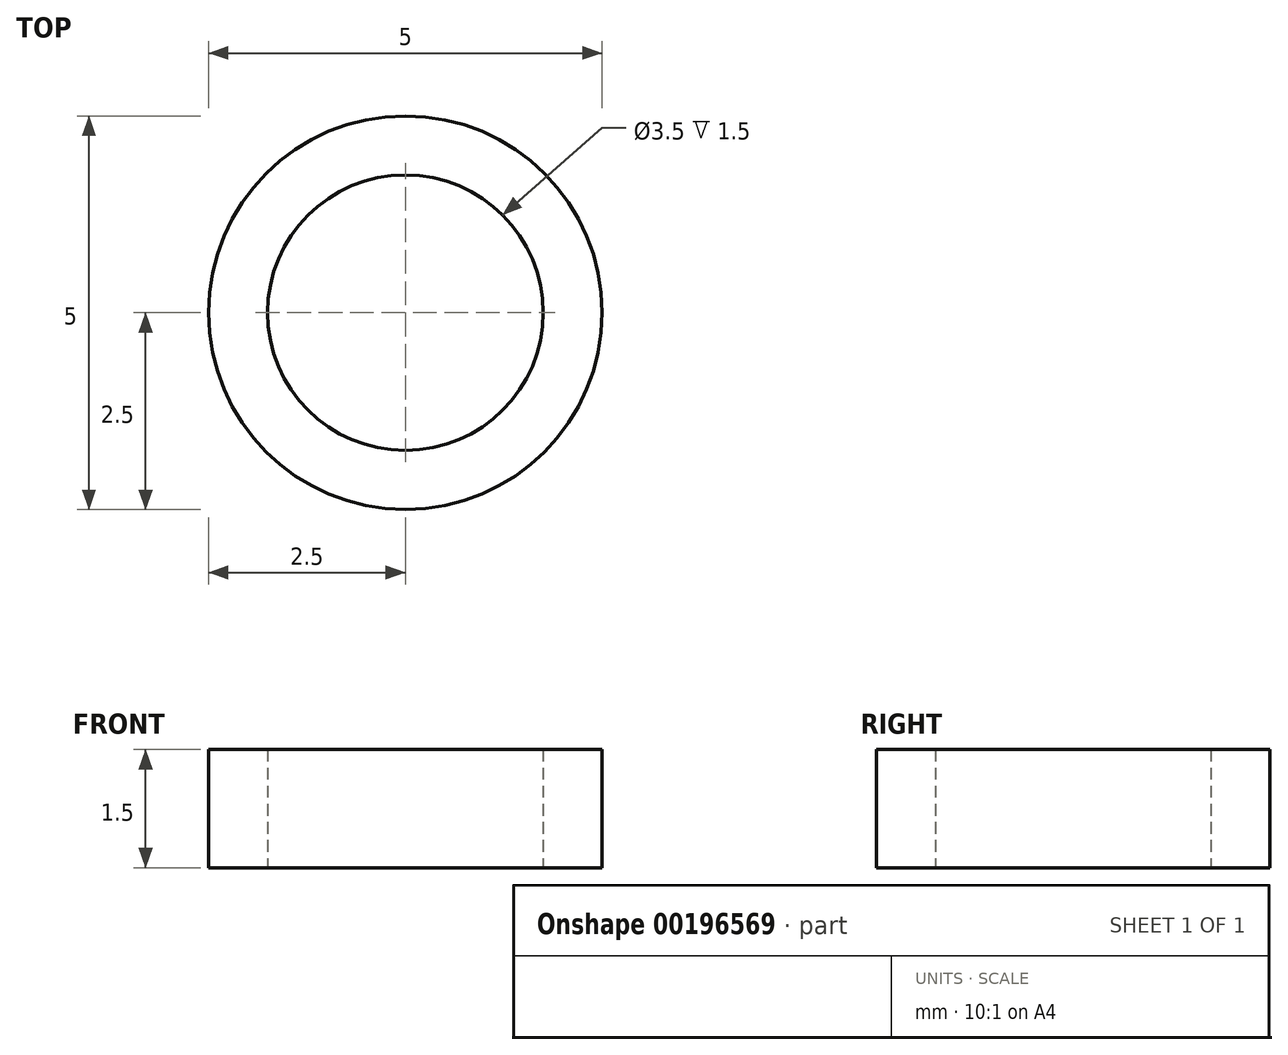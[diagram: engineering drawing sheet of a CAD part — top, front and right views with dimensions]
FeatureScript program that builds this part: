
annotation { "Feature Type Name" : "Feature", "Feature Type Description" : "" }
export const myFeature = defineFeature(function(context is Context, id is Id, definition is map)
    precondition{}
    {
        {
            var Q0;
            Q0=qCreatedBy(makeId("Top.planeOp"),FACE);
            var sketch = newSketch(context, id + "F0", { "sketchPlane" : qUnion([Q0])});
            skCircle(sketch, "E0", {"center": v(0, 0) * mm, "radius": 1.75 * mm});
            skCircle(sketch, "E1", {"center": v(0, 0) * mm, "radius": 2.5 * mm});
            skSolve(sketch);
        }
        {
            var Q0;
            Q0 = qSketchRegion(id + "F0", true);
            extrude(context, id + "F1", {"entities" : qUnion([Q0]), "depth" : 1.5 * mm});
        }
    });
